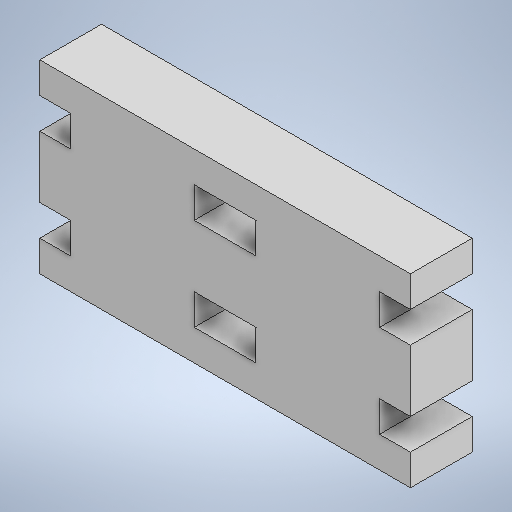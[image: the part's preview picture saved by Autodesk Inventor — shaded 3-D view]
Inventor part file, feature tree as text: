
AUTODESK INVENTOR PART (.ipt)
format: ipt  version: 2025.1 (Build 291241020, 241B)  size: 233,984 bytes
history: native  units: in
note: dims shown in document units (in); Inventor stores cm internally (conversion verified against a paired STEP export)
features: sketch x2, extrude x1
ambient origin geometry x8: Origin, YZ Plane, XZ Plane, XY Plane, X Axis, Y Axis, Z Axis, Center Point
bodies: Solid1 (feature_tree)
feature tree (3):
  extrude  "Extrusion1"  Depth=3.0in
  sketch  "Sketch1"  dims[d0=6.0in d1=3.0in]
  sketch  "Sketch Rectangular Pattern1"  dims[d2=0.5in d3=0.5in d4=0.5in d5=0.5in d6=2.5in d7=1.0in d8=0.5in d9=0.5in d10=0.7874in d12=1.5in d13=0.3937in d15=1.0in d17=1.0in d18=0.5in d19=0.5in d20=0.5in d21=1.0in d22=0.0in]
